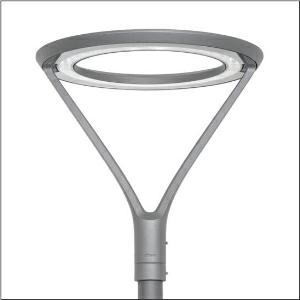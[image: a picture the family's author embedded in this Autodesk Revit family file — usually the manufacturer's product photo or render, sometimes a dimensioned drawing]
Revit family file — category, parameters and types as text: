
# Revit family: dl_r__20___st1_2a_5xa51283wa008p_0b9f
name_source: partatom
category: Lighting Fixtures
units: mm (PartAtom-declared; Revit-internal decimal feet)

## family parameters
Cut with Voids When Loaded = No
Host = Face
Light Source = No
Part Type = Normal
Room Calculation Point = No
Round Connector Dimension = Use Diameter
Shared = No

## types (1)
- --- (1 x LED, 4200 lm, 34.3 W, 3000K)
    Apparent Load = 34 VA
    CIE Flux Codes = 32 72 97 100 100
    Color Rendering = 70
    Color Temperature = 3000K
    Default Elevation = 1800 mm
    Description = DL® 20, mast luminaire, primary light control with reflector, highly specular, primary optical cover: cover, of toughened safety glass of clear glass with excellent transmission level, light distribution: ST1.2a, light emission: direct distribution, primary light characteristic: asymmetric, installation type: post-top, LED, High Power LED, rated luminous flux: 4.180lm, luminous efficacy: 79lm/W, light colour: 730, colour temperature: 3000K, control gear: ECG Plus, control: overheat protection, power reduction, digital communication interface, constant luminous flux control, time-dependent luminous flux control, flexible luminous flux parameterisation, electronic power reduction, mains connection: 230..240V, 50/60Hz, connection cable pre-assembled, cable length: 5m, start of lifetime: 53W, end of service life: 54W, reduction: 24W, luminaire housing, upper part, of cast aluminium, powder-coated, Siteco® metallic grey (DB 702S), diameter: 690mm, height: 690mm, spigot size: 76mm (post-top), luminaire housing, of cast aluminium, powder-coated, Siteco® metallic grey (DB 702S), equipment: Power, protection rating (complete): IP66, insulation class (complete): insulation class II (safety insulation), certification: CE, ENEC, VDE, impact resistance: IK08, permissible operating ambient temperature: -25..+30°C, standard-compliant lighting for roads and squares, packaging unit: 1 piece

Light Distribution: ST1.2a
    Height = 690 mm
    Lamp = 1 x LED
    Lamp Light Flux = 4200 lm
    Lamp Power = 34.3 W
    Lamp count = 1
    Length = 690 mm
    Luminous efficacy = 122 lm/W
    Manufacturer = Siteco
    ModVariant = No
    Model = 5XA51283WA008P
    Number of Poles = 1
    OnlyDefault = Yes
    Power Factor = 1
    Product Name = DL® 20 | ST1.2a
    Product group = mast luminaire | pylon top
    ProductGroupID = 6100
    Protection Class = Protection class II
    Protection Degree = IP 66
    RLX_Detail_Level = 1
    RLX_Emergency_Light_Flux = 0 lm
    RLX_Emergency_Type = 0
    RLX_Emergency_Type_DB = No
    RlxData = <blob elided: 206721 chars, md5=e2426478>
    Socket = socket
    Standby Power = 0 W
    System Light Flux = 4200 lm
    System Power = 34 W
    Type Comments = factory setting: luminous flux: 100 % | dim-lin: 254 | 464 mA
    Type Image = l_1006001.jpg
    URL = http://relux.com
    VarID = @adj_028353
    Voltage = 0 V
    Weight = 0.00 kg
    Width = 0 mm  [stored 0 ft]

note: [stored X ft] marks values corroborated as IEEE doubles in the binary element streams (Revit-internal decimal feet)

## geometry (parser evidence)
native form markers: Blend x4, Sweep x10
no freeform markers — native parametric forms only
